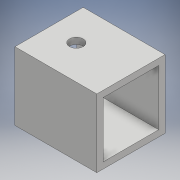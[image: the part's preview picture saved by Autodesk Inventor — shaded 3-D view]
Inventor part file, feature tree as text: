
AUTODESK INVENTOR PART (.ipt)
format: ipt  version: 2018.2 (Build 222227000, 227)  size: 105,472 bytes
history: native  units: mm
features: extrude x2, sketch x2, other x1
ambient origin geometry x8: Origin, YZ Plane, XZ Plane, XY Plane, X Axis, Y Axis, Z Axis, Center Point
bodies: Body1 (feature_tree)
feature tree (5):
  other  "ソリッド1"
  extrude  "押し出し1"  Depth=25.0mm
  extrude  "押し出し2"  Depth=25.0mm
  sketch  "スケッチ1"
  sketch  "スケッチ2"
